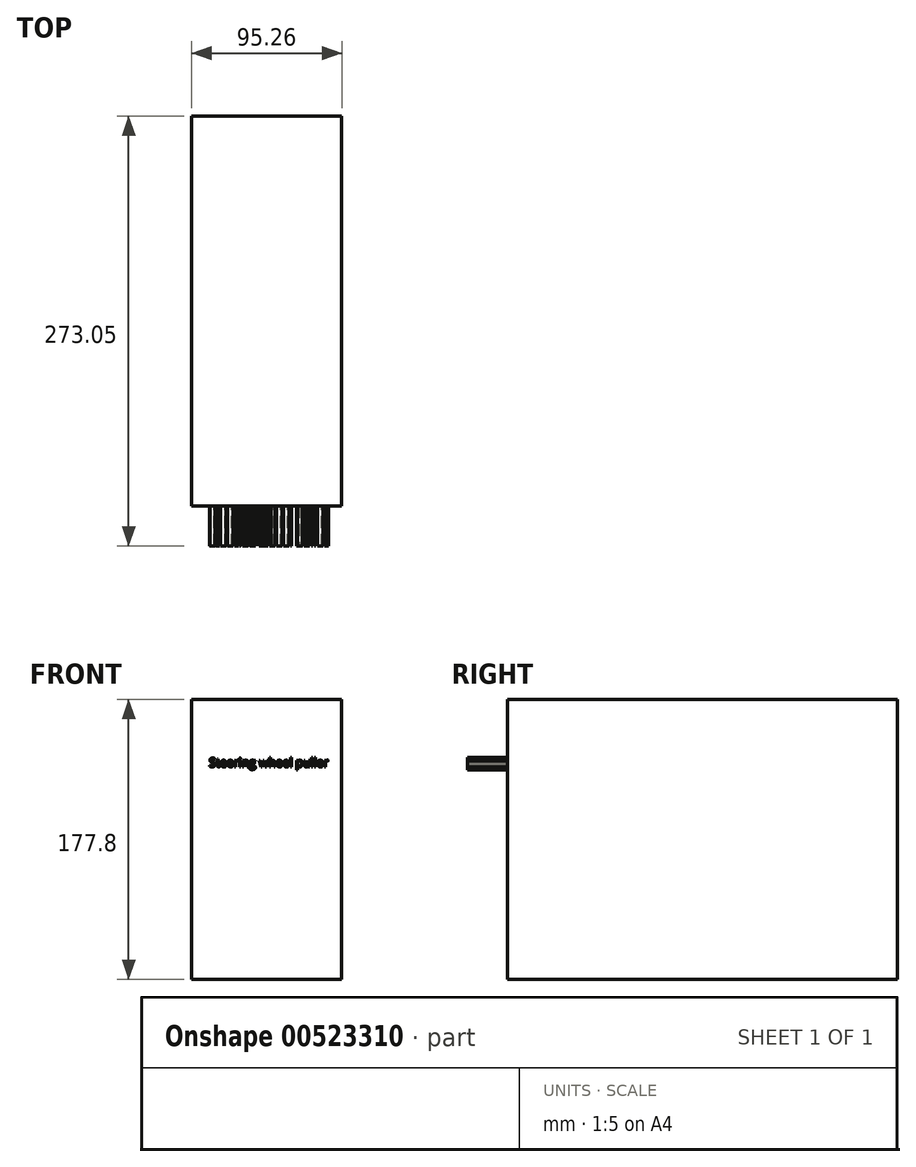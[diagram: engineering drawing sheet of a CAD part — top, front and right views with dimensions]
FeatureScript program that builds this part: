
annotation { "Feature Type Name" : "Feature", "Feature Type Description" : "" }
export const myFeature = defineFeature(function(context is Context, id is Id, definition is map)
    precondition{}
    {
        {
            var Q0;
            Q0=qCreatedBy(makeId("Front.planeOp"),FACE);
            var sketch = newSketch(context, id + "F0", { "sketchPlane" : qUnion([Q0])});
            skLineSegment(sketch, "E0.bottom", {"start": v(47.62, 88.9) * mm, "end": v(-47.63, 88.9) * mm});
            skLineSegment(sketch, "E0.top", {"start": v(47.63, -88.9) * mm, "end": v(-47.62, -88.9) * mm});
            skLineSegment(sketch, "E0.left", {"start": v(47.62, 88.9) * mm, "end": v(47.63, -88.9) * mm});
            skLineSegment(sketch, "E0.right", {"start": v(-47.63, 88.9) * mm, "end": v(-47.62, -88.9) * mm});
            skPoint(sketch, "E0.middle", {"position": v(0, 0) * mm});
            skSolve(sketch);
        }
        {
            var Q0;
            Q0=makeQuery(id+"F0.imprint","IMPRINT",FACE,{"disambiguationData":[TD([[makeQuery(id+"F0.imprint","IMPRINT",EDGE,{"derivedFrom":sQuery(id+"F0.wireOp",EDGE,"E0.bottom")}),1.0]])]});
            extrude(context, id + "F1", {"entities" : qUnion([Q0]), "depth" : 247.65 * mm, "offsetDistance" : 25.4 * mm});
        }
        {
            var Q0;
            Q0=makeQuery(id+"F1.opExtrude","CAP_FACE",FACE,{"disambiguationData":[OSD([sQuery(id+"F0.wireOp",EDGE,"E0.bottom"),sQuery(id+"F0.wireOp",EDGE,"E0.top"),sQuery(id+"F0.wireOp",EDGE,"E0.left"),sQuery(id+"F0.wireOp",EDGE,"E0.right")])],"isStart":false});
            var sketch = newSketch(context, id + "F2", { "sketchPlane" : qUnion([Q0])});
            skText(sketch, "E1", { "text": "Steering wheel puller", "fontName": "OpenSans-Regular.ttf"});
            const initialGuessF2  = {"E1": [-0.03663, 0.04616, 1, 0, 0.00555]};
            skSetInitialGuess(sketch, initialGuessF2);
            skSolve(sketch);
        }
        {
            var Q0;
            Q0 = qSketchRegion(id + "F2", true);
            extrude(context, id + "F3", {"entities" : qUnion([Q0]), "operationType" : NewBodyOperationType.ADD, "depth" : 25.4 * mm, "offsetDistance" : 25.4 * mm});
        }
    });
